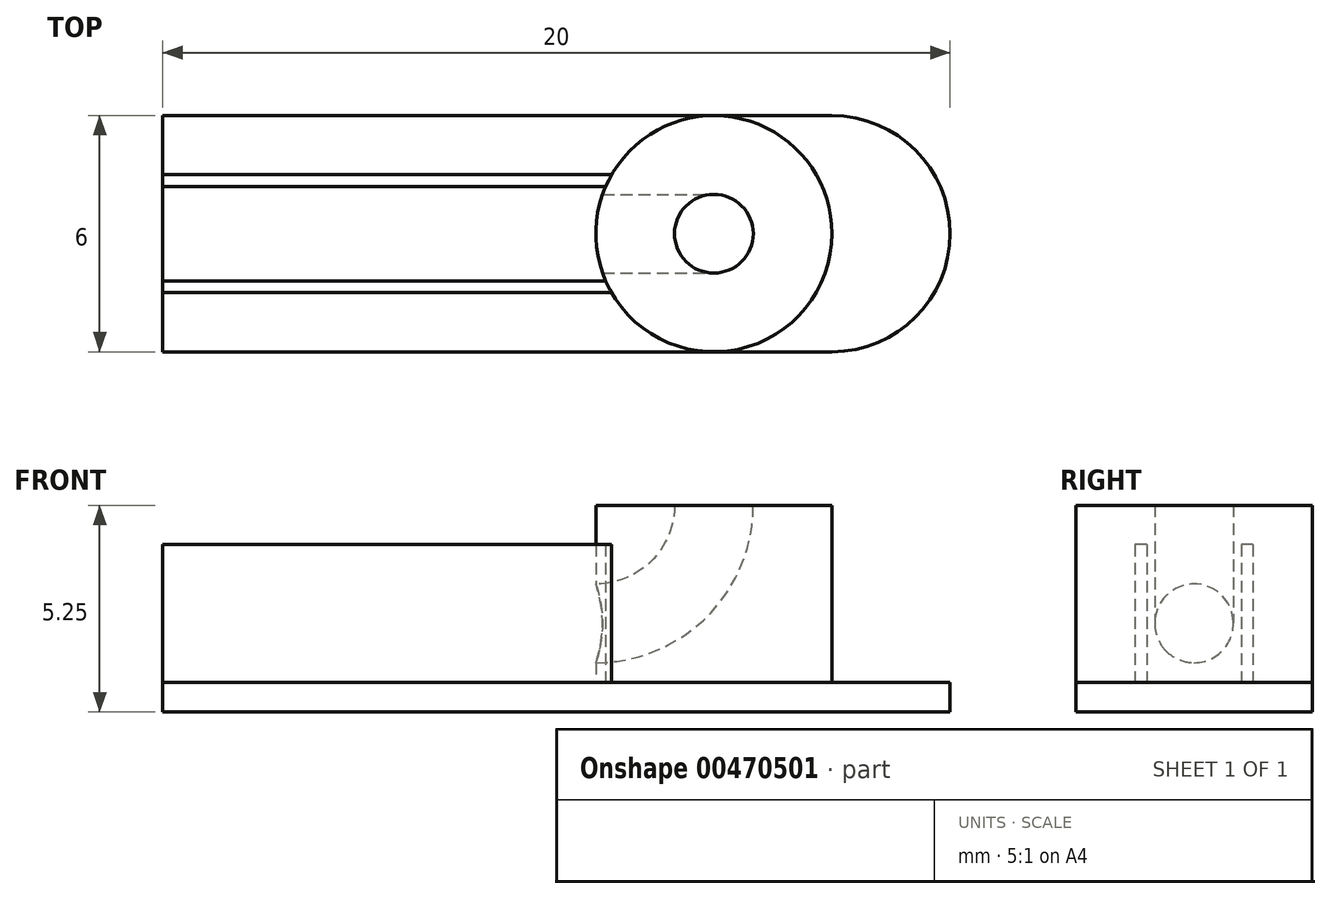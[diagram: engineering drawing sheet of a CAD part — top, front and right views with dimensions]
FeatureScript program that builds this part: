
annotation { "Feature Type Name" : "Feature", "Feature Type Description" : "" }
export const myFeature = defineFeature(function(context is Context, id is Id, definition is map)
    precondition{}
    {
        {
            var Q0;
            Q0=qCreatedBy(makeId("Top.planeOp"),FACE);
            var sketch = newSketch(context, id + "F0", { "sketchPlane" : qUnion([Q0])});
            skLineSegment(sketch, "E0.bottom", {"start": v(-14, 3) * mm, "end": v(6, 3) * mm});
            skLineSegment(sketch, "E0.top", {"start": v(-14, -3) * mm, "end": v(6, -3) * mm});
            skLineSegment(sketch, "E0.left", {"start": v(-14, 3) * mm, "end": v(-14, -3) * mm});
            skLineSegment(sketch, "E0.right", {"start": v(6, 3) * mm, "end": v(6, -3) * mm});
            skSolve(sketch);
        }
        {
            var Q0;
            Q0=makeQuery(id+"F0.imprint","IMPRINT",FACE,{"disambiguationData":[TD([[makeQuery(id+"F0.imprint","IMPRINT",EDGE,{"derivedFrom":sQuery(id+"F0.wireOp",EDGE,"E0.bottom")}),-1.0]])]});
            extrude(context, id + "F1", {"entities" : qUnion([Q0]), "depth" : 0.75 * mm});
        }
        {
            var Q0;
            Q0=makeQuery(id+"F1.opExtrude","CAP_FACE",FACE,{"disambiguationData":[OSD([sQuery(id+"F0.wireOp",EDGE,"E0.bottom"),sQuery(id+"F0.wireOp",EDGE,"E0.top"),sQuery(id+"F0.wireOp",EDGE,"E0.left"),sQuery(id+"F0.wireOp",EDGE,"E0.right")])],"isStart":false});
            var sketch = newSketch(context, id + "F2", { "sketchPlane" : qUnion([Q0])});
            skCircle(sketch, "E1", {"center": v(0, 0) * mm, "radius": 3 * mm});
            skSolve(sketch);
        }
        {
            var Q0;
            {var subQ0=sQuery(id+"F2.wireOp",EDGE,"E1");var subQ1=makeQuery(id+"F2.imprint","INTERSECT",VERTEX,{"derivedFrom":[makeQuery(id+"F1.opExtrude","CAP_EDGE",EDGE,{"disambiguationData":[OSD([sQuery(id+"F0.wireOp",EDGE,"E0.bottom")])],"isStart":false}),subQ0]});Q0=makeQuery(id+"F2.imprint","IMPRINT",FACE,{"disambiguationData":[TD([[makeQuery(id+"F2.imprint","IMPRINT",EDGE,{"disambiguationData":[TD([[subQ1,-1.0]])],"derivedFrom":subQ0}),1.0]])]});}
            extrude(context, id + "F3", {"entities" : qUnion([Q0]), "operationType" : NewBodyOperationType.ADD, "depth" : 4.5 * mm});
        }
        {
            var Q0;
            Q0=makeQuery(id+"F3.opExtrude","CAP_FACE",FACE,{"disambiguationData":[OSD([sQuery(id+"F2.wireOp",EDGE,"E1")])],"isStart":false});
            var sketch = newSketch(context, id + "F4", { "sketchPlane" : qUnion([Q0])});
            skLineSegment(sketch, "E2", {"start": v(-3, 0) * mm, "end": v(-3, -5.92) * mm, "construction": true});
            skCircle(sketch, "E3", {"center": v(0, 0) * mm, "radius": 1 * mm});
            skSolve(sketch);
        }
        {
            var Q0;
            Q0=makeQuery(id+"F4.imprint","IMPRINT",FACE,{"disambiguationData":[TD([[makeQuery(id+"F4.imprint","IMPRINT",EDGE,{"derivedFrom":sQuery(id+"F4.wireOp",EDGE,"E3")}),1.0]])]});
            var Q1;
            Q1=sQuery(id+"F4.wireOp",EDGE,"E3");
            var Q2;
            Q2=sQuery(id+"F4.wireOp",EDGE,"E2");
            revolve(context, id + "F5", {"operationType" : NewBodyOperationType.REMOVE, "entities" : qUnion([Q0]), "surfaceEntities" : qUnion([Q1]), "axis" : qUnion([Q2]), "revolveType" : RevolveType.FULL, "oppositeDirection" : true});
        }
        {
            var Q0;
            Q0=makeQuery(id+"F1.opExtrude","SWEPT_EDGE",EDGE,{"disambiguationData":[OSD([sQuery(id+"F0.wireOp",EDGE,"E0.top"),sQuery(id+"F0.wireOp",EDGE,"E0.right")])]});
            var Q1;
            Q1=makeQuery(id+"F1.opExtrude","SWEPT_EDGE",EDGE,{"disambiguationData":[OSD([sQuery(id+"F0.wireOp",EDGE,"E0.bottom"),sQuery(id+"F0.wireOp",EDGE,"E0.right")])]});
            fillet(context, id + "F6", {"entities" : qUnion([Q0, Q1]), "radius" : 3 * mm, "tangentPropagation" : true, "allowEdgeOverflow" : false});
        }
        {
            var Q0;
            {var subQ0=sQuery(id+"F0.wireOp",EDGE,"E0.left");var subQ1=sQuery(id+"F0.wireOp",EDGE,"E0.top");var subQ2=sQuery(id+"F0.wireOp",EDGE,"E0.bottom");var subQ3=makeQuery(id+"F1.opExtrude","CAP_FACE",FACE,{"disambiguationData":[OSD([subQ2,subQ1,subQ0,sQuery(id+"F0.wireOp",EDGE,"E0.right")])],"isStart":false});Q0=makeQuery(id+"F3.boolean.opBoolean","SPLIT",FACE,{"disambiguationData":[TD([makeQuery(id+"F1.opExtrude","SWEPT_FACE",FACE,{"disambiguationData":[OSD([subQ0])]})])],"derivedFrom":subQ3});}
            var sketch = newSketch(context, id + "F7", { "sketchPlane" : qUnion([Q0])});
            skLineSegment(sketch, "E4.bottom", {"start": v(-14, 1.5) * mm, "end": v(-2, 1.5) * mm});
            skLineSegment(sketch, "E4.top", {"start": v(-14, 1.2) * mm, "end": v(-2, 1.2) * mm});
            skLineSegment(sketch, "E4.left", {"start": v(-14, 1.5) * mm, "end": v(-14, 1.2) * mm});
            skLineSegment(sketch, "E4.right", {"start": v(-2, 1.5) * mm, "end": v(-2, 1.2) * mm});
            skLineSegment(sketch, "E5.bottom", {"start": v(-14, -1.2) * mm, "end": v(-2, -1.2) * mm});
            skLineSegment(sketch, "E5.top", {"start": v(-14, -1.5) * mm, "end": v(-2, -1.5) * mm});
            skLineSegment(sketch, "E5.left", {"start": v(-14, -1.2) * mm, "end": v(-14, -1.5) * mm});
            skLineSegment(sketch, "E5.right", {"start": v(-2, -1.2) * mm, "end": v(-2, -1.5) * mm});
            skSolve(sketch);
        }
        {
            var Q0;
            {var subQ0=sQuery(id+"F7.wireOp",EDGE,"E4.left");Q0=makeQuery(id+"F7.imprint","IMPRINT",FACE,{"disambiguationData":[TD([[makeQuery(id+"F7.imprint","IMPRINT",EDGE,{"derivedFrom":subQ0}),1.0]])]});}
            var Q1;
            {var subQ0=sQuery(id+"F7.wireOp",EDGE,"E5.left");Q1=makeQuery(id+"F7.imprint","IMPRINT",FACE,{"disambiguationData":[TD([[makeQuery(id+"F7.imprint","IMPRINT",EDGE,{"derivedFrom":subQ0}),1.0]])]});}
            extrude(context, id + "F8", {"entities" : qUnion([Q0, Q1]), "operationType" : NewBodyOperationType.ADD, "depth" : 3.5 * mm});
        }
    });
